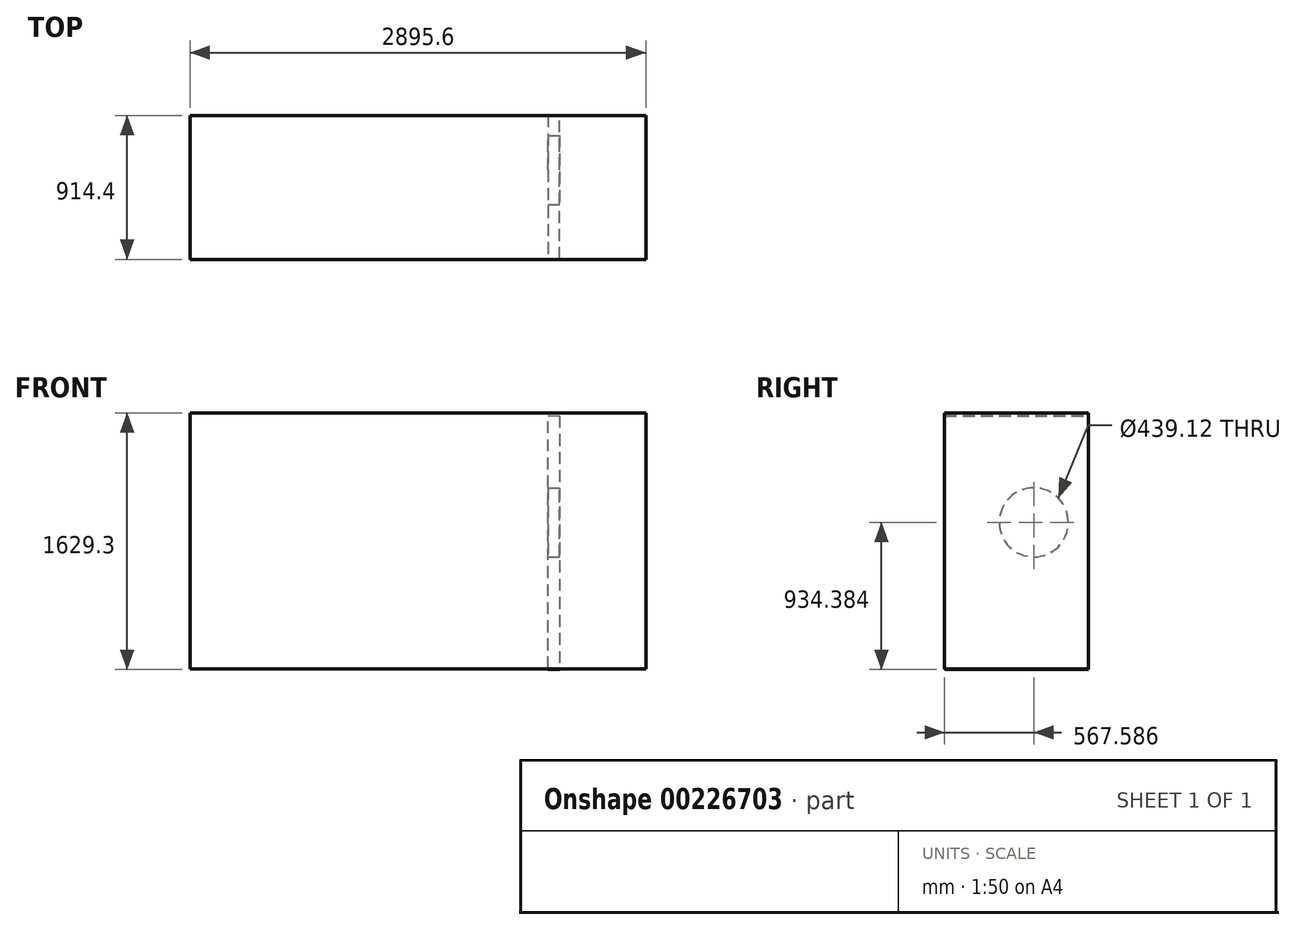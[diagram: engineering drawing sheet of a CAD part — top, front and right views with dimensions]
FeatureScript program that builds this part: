
annotation { "Feature Type Name" : "Feature", "Feature Type Description" : "" }
export const myFeature = defineFeature(function(context is Context, id is Id, definition is map)
    precondition{}
    {
        {
            var Q0;
            Q0=qCreatedBy(makeId("Front.planeOp"),FACE);
            var sketch = newSketch(context, id + "F0", { "sketchPlane" : qUnion([Q0])});
            skLineSegment(sketch, "E0.bottom", {"start": v(-1448.92, 833.6) * mm, "end": v(1446.68, 833.6) * mm});
            skLineSegment(sketch, "E0.top", {"start": v(-1448.92, -792) * mm, "end": v(1446.68, -792) * mm});
            skLineSegment(sketch, "E0.left", {"start": v(-1448.92, 833.6) * mm, "end": v(-1448.92, -792) * mm});
            skLineSegment(sketch, "E0.right", {"start": v(1446.68, 833.6) * mm, "end": v(1446.68, -792) * mm});
            skSolve(sketch);
        }
        {
            var Q0;
            Q0 = qSketchRegion(id + "F0", true);
            extrude(context, id + "F1", {"entities" : qUnion([Q0]), "depth" : 914.4 * mm});
        }
        {
            var Q0;
            Q0=makeQuery(id+"F1.opExtrude","CAP_FACE",FACE,{"disambiguationData":[OSD([sQuery(id+"F0.wireOp",EDGE,"E0.bottom"),sQuery(id+"F0.wireOp",EDGE,"E0.top"),sQuery(id+"F0.wireOp",EDGE,"E0.left"),sQuery(id+"F0.wireOp",EDGE,"E0.right")])],"isStart":true});
            shell(context, id + "F2", {"entities" : qUnion([Q0]), "thickness" : 2.54 * mm});
        }
        {
            var Q0;
            Q0=qCreatedBy(makeId("Front.planeOp"),FACE);
            var sketch = newSketch(context, id + "F3", { "sketchPlane" : qUnion([Q0])});
            skLineSegment(sketch, "E1", {"start": v(899.38, 815.1) * mm, "end": v(899.38, -795.71) * mm});
            skLineSegment(sketch, "E2", {"start": v(899.38, -795.71) * mm, "end": v(823.98, -795.71) * mm});
            skLineSegment(sketch, "E3", {"start": v(823.98, -795.71) * mm, "end": v(823.98, 817.45) * mm});
            skLineSegment(sketch, "E4", {"start": v(823.98, 817.45) * mm, "end": v(899.38, 815.1) * mm});
            skSolve(sketch);
        }
        {
            var Q0;
            Q0 = qSketchRegion(id + "F3", true);
            extrude(context, id + "F4", {"entities" : qUnion([Q0]), "operationType" : NewBodyOperationType.ADD, "depth" : 911.86 * mm});
        }
        {
            var Q0;
            {var subQ1=sQuery(id+"F3.wireOp",EDGE,"E1");var subQ2=sQuery(id+"F0.wireOp",EDGE,"E0.top");Q0=makeQuery(id+"F4.boolean.opBoolean","SPLIT",FACE,{"disambiguationData":[TD([makeQuery(id+"F2.opShell","OFFSET_FACE",FACE,{"disambiguationData":[OSD([subQ2])]})])],"derivedFrom":makeQuery(id+"F4.opExtrude","SWEPT_FACE",FACE,{"disambiguationData":[OSD([subQ1])]})});}
            var sketch = newSketch(context, id + "F5", { "sketchPlane" : qUnion([Q0])});
            skCircle(sketch, "E5", {"center": v(-346.81, 138.67) * mm, "radius": 219.56 * mm});
            skSolve(sketch);
        }
        {
            var Q0;
            Q0=makeQuery(id+"F5.imprint","IMPRINT",FACE,{"disambiguationData":[TD([[makeQuery(id+"F5.imprint","IMPRINT",EDGE,{"derivedFrom":sQuery(id+"F5.wireOp",EDGE,"E5")}),1.0]])]});
            extrude(context, id + "F6", {"entities" : qUnion([Q0]), "operationType" : NewBodyOperationType.REMOVE, "oppositeDirection" : true, "depth" : 111.76 * mm});
        }
    });
